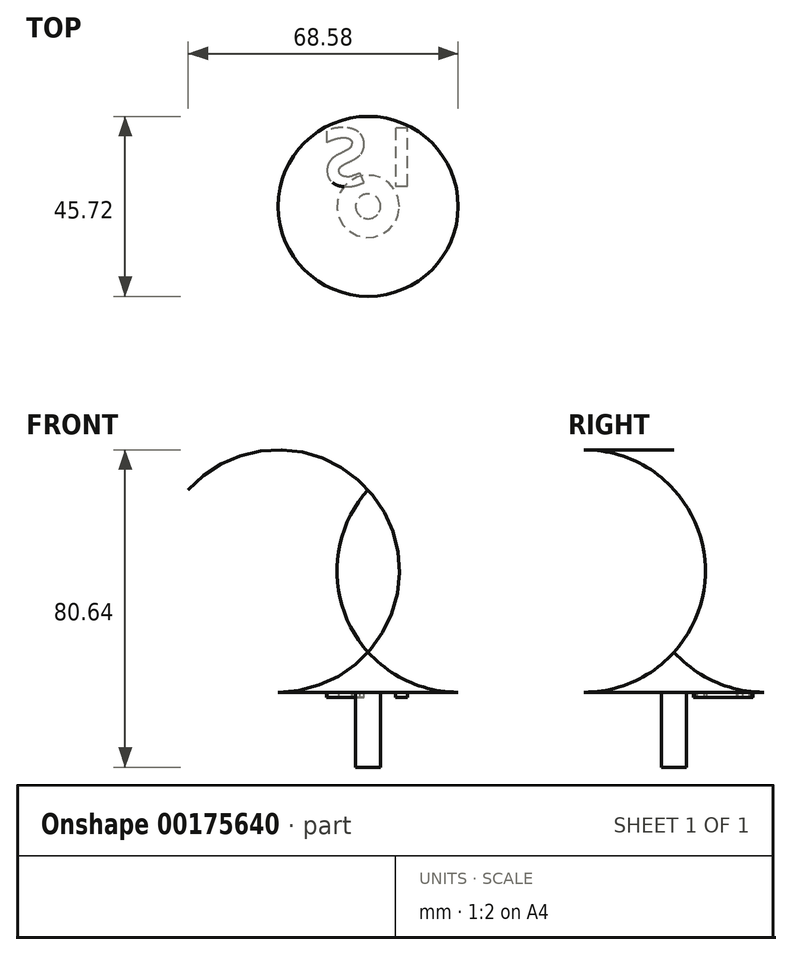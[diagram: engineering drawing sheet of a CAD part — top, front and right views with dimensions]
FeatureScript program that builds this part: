
annotation { "Feature Type Name" : "Feature", "Feature Type Description" : "" }
export const myFeature = defineFeature(function(context is Context, id is Id, definition is map)
    precondition{}
    {
        {
            var Q0;
            Q0=qCreatedBy(makeId("Front.planeOp"),FACE);
            var sketch = newSketch(context, id + "F0", { "sketchPlane" : qUnion([Q0])});
            skLineSegment(sketch, "E0", {"start": v(0, 0) * mm, "end": v(0, 10.16) * mm});
            skLineSegment(sketch, "E1", {"start": v(22.86, 0) * mm, "end": v(0, 0) * mm});
            skArc(sketch, "E2", {"start": v(0, 10.16) * mm, "mid": v(10.35, 2.65) * mm, "end": v(22.86, 0) * mm});
            skSolve(sketch);
        }
        {
            var Q0;
            Q0=makeQuery(id+"F0.imprint","IMPRINT",FACE,{"disambiguationData":[TD([[makeQuery(id+"F0.imprint","IMPRINT",EDGE,{"derivedFrom":sQuery(id+"F0.wireOp",EDGE,"E0")}),-1.0]])]});
            var Q1;
            Q1=sQuery(id+"F0.wireOp",EDGE,"E0");
            revolve(context, id + "F1", {"entities" : qUnion([Q0]), "axis" : qUnion([Q1]), "revolveType" : RevolveType.FULL});
        }
        {
            var Q0;
            Q0=makeQuery(id+"F1.opRevolve","SWEPT_FACE",FACE,{"disambiguationData":[OSD([sQuery(id+"F0.wireOp",EDGE,"E1")])]});
            var sketch = newSketch(context, id + "F2", { "sketchPlane" : qUnion([Q0])});
            skCircle(sketch, "E3", {"center": v(0, 0) * mm, "radius": 3.18 * mm});
            skSolve(sketch);
        }
        {
            var Q0;
            Q0=makeQuery(id+"F2.imprint","IMPRINT",FACE,{"disambiguationData":[TD([[makeQuery(id+"F2.imprint","IMPRINT",EDGE,{"derivedFrom":sQuery(id+"F2.wireOp",EDGE,"E3")}),1.0]])]});
            extrude(context, id + "F3", {"entities" : qUnion([Q0]), "operationType" : NewBodyOperationType.ADD, "depth" : 19.05 * mm});
        }
        {
            var Q0;
            Q0=makeQuery(id+"F1.opRevolve","SWEPT_FACE",FACE,{"disambiguationData":[OSD([sQuery(id+"F0.wireOp",EDGE,"E1")])]});
            var sketch = newSketch(context, id + "F4", { "sketchPlane" : qUnion([Q0])});
            skText(sketch, "E4", { "text": "S I", "fontName": "OpenSans-Bold.ttf"});
            const initialGuessF4  = {"E4": [-0.01153, -0.01982, 1, 0, 0.01477]};
            skSetInitialGuess(sketch, initialGuessF4);
            skSolve(sketch);
        }
        {
            var Q0;
            Q0 = qSketchRegion(id + "F4", true);
            extrude(context, id + "F5", {"entities" : qUnion([Q0]), "operationType" : NewBodyOperationType.ADD, "depth" : 1.27 * mm});
        }
    });
